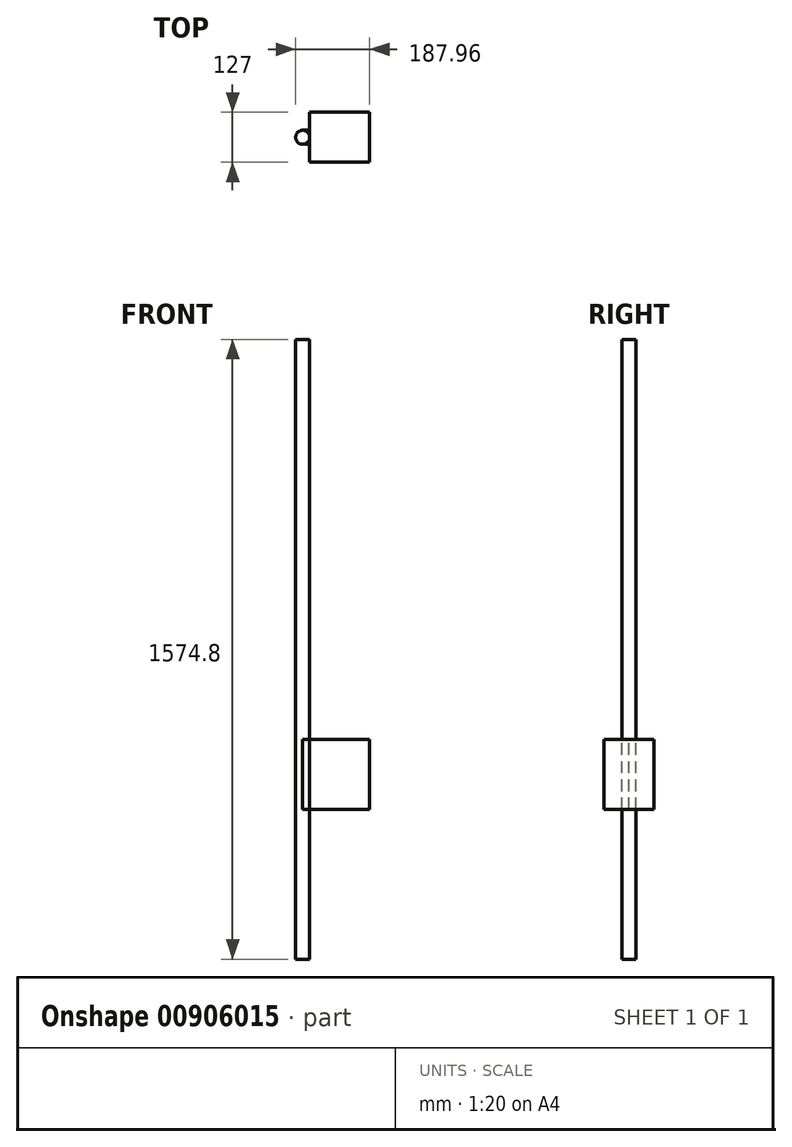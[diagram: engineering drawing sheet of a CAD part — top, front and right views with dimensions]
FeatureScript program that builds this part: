
annotation { "Feature Type Name" : "Feature", "Feature Type Description" : "" }
export const myFeature = defineFeature(function(context is Context, id is Id, definition is map)
    precondition{}
    {
        {
            var Q0;
            Q0=qCreatedBy(makeId("Top.planeOp"),FACE);
            var sketch = newSketch(context, id + "F0", { "sketchPlane" : qUnion([Q0])});
            skCircle(sketch, "E0", {"center": v(0, 0) * mm, "radius": 17.78 * mm});
            skSolve(sketch);
        }
        {
            var Q0;
            Q0=makeQuery(id+"F0.imprint","IMPRINT",FACE,{"disambiguationData":[TD([[makeQuery(id+"F0.imprint","IMPRINT",EDGE,{"derivedFrom":sQuery(id+"F0.wireOp",EDGE,"E0")}),1.0]])]});
            extrude(context, id + "F1", {"entities" : qUnion([Q0]), "endBound" : BoundingType.SYMMETRIC, "oppositeDirection" : true, "depth" : 1574.8 * mm, "offsetDistance" : 25.4 * mm});
        }
        {
            var Q0;
            Q0=qCreatedBy(makeId("Front.planeOp"),FACE);
            var sketch = newSketch(context, id + "F2", { "sketchPlane" : qUnion([Q0])});
            skLineSegment(sketch, "E1.bottom", {"start": v(17.78, -228.6) * mm, "end": v(170.18, -228.6) * mm});
            skLineSegment(sketch, "E1.top", {"start": v(17.78, -406.4) * mm, "end": v(170.18, -406.4) * mm});
            skLineSegment(sketch, "E1.left", {"start": v(17.78, -228.6) * mm, "end": v(17.78, -406.4) * mm});
            skLineSegment(sketch, "E1.right", {"start": v(170.18, -228.6) * mm, "end": v(170.18, -406.4) * mm});
            skLineSegment(sketch, "E2", {"start": v(17.78, 787.4) * mm, "end": v(17.78, -787.4) * mm});
            skSolve(sketch);
        }
        {
            var Q0;
            Q0=makeQuery(id+"F2.imprint","IMPRINT",FACE,{"disambiguationData":[TD([[makeQuery(id+"F2.imprint","IMPRINT",EDGE,{"derivedFrom":sQuery(id+"F2.wireOp",EDGE,"E1.bottom")}),-1.0]])]});
            extrude(context, id + "F3", {"entities" : qUnion([Q0]), "operationType" : NewBodyOperationType.ADD, "endBound" : BoundingType.SYMMETRIC, "depth" : 127 * mm, "offsetDistance" : 25.4 * mm});
        }
        {
            var Q0;
            Q0=makeQuery(id+"F3.opExtrude","SWEPT_FACE",FACE,{"disambiguationData":[OSD([sQuery(id+"F2.wireOp",EDGE,"E1.bottom")])]});
            var sketch = newSketch(context, id + "F4", { "sketchPlane" : qUnion([Q0])});
            skCircle(sketch, "E3.0", {"center": v(0, 0) * mm, "radius": 17.78 * mm});
            skLineSegment(sketch, "E4.0", {"start": v(17.78, -63.5) * mm, "end": v(17.78, 63.5) * mm});
            skLineSegment(sketch, "E5", {"start": v(0, 0) * mm, "end": v(0, 17.78) * mm});
            skLineSegment(sketch, "E6", {"start": v(0, 17.78) * mm, "end": v(0, 17.78) * mm});
            skLineSegment(sketch, "E7", {"start": v(0, 0) * mm, "end": v(0, -17.78) * mm});
            skLineSegment(sketch, "E8", {"start": v(0, -17.78) * mm, "end": v(17.78, -17.78) * mm});
            skLineSegment(sketch, "E9", {"start": v(17.78, -17.78) * mm, "end": v(17.78, 17.78) * mm});
            skLineSegment(sketch, "E10", {"start": v(0, 17.78) * mm, "end": v(17.78, 17.78) * mm});
            skLineSegment(sketch, "E11", {"start": v(0, -17.78) * mm, "end": v(0, -17.78) * mm});
            skSolve(sketch);
        }
        {
            var Q0;
            {var subQ0=sQuery(id+"F4.wireOp",EDGE,"E8");Q0=makeQuery(id+"F4.imprint","IMPRINT",FACE,{"disambiguationData":[TD([[makeQuery(id+"F4.imprint","IMPRINT",EDGE,{"derivedFrom":subQ0}),1.0]])]});}
            var Q1;
            {var subQ0=sQuery(id+"F4.wireOp",EDGE,"E10");Q1=makeQuery(id+"F4.imprint","IMPRINT",FACE,{"disambiguationData":[TD([[makeQuery(id+"F4.imprint","IMPRINT",EDGE,{"derivedFrom":subQ0}),-1.0]])]});}
            var Q2;
            Q2=makeQuery(id+"F3.opExtrude","SWEPT_FACE",FACE,{"disambiguationData":[OSD([sQuery(id+"F2.wireOp",EDGE,"E1.top")])]});
            extrude(context, id + "F5", {"entities" : qUnion([Q0, Q1]), "endBound" : BoundingType.UP_TO_SURFACE, "oppositeDirection" : true, "depth" : 25.4 * mm, "endBoundEntityFace" : qUnion([Q2]), "offsetDistance" : 25.4 * mm});
        }
    });
